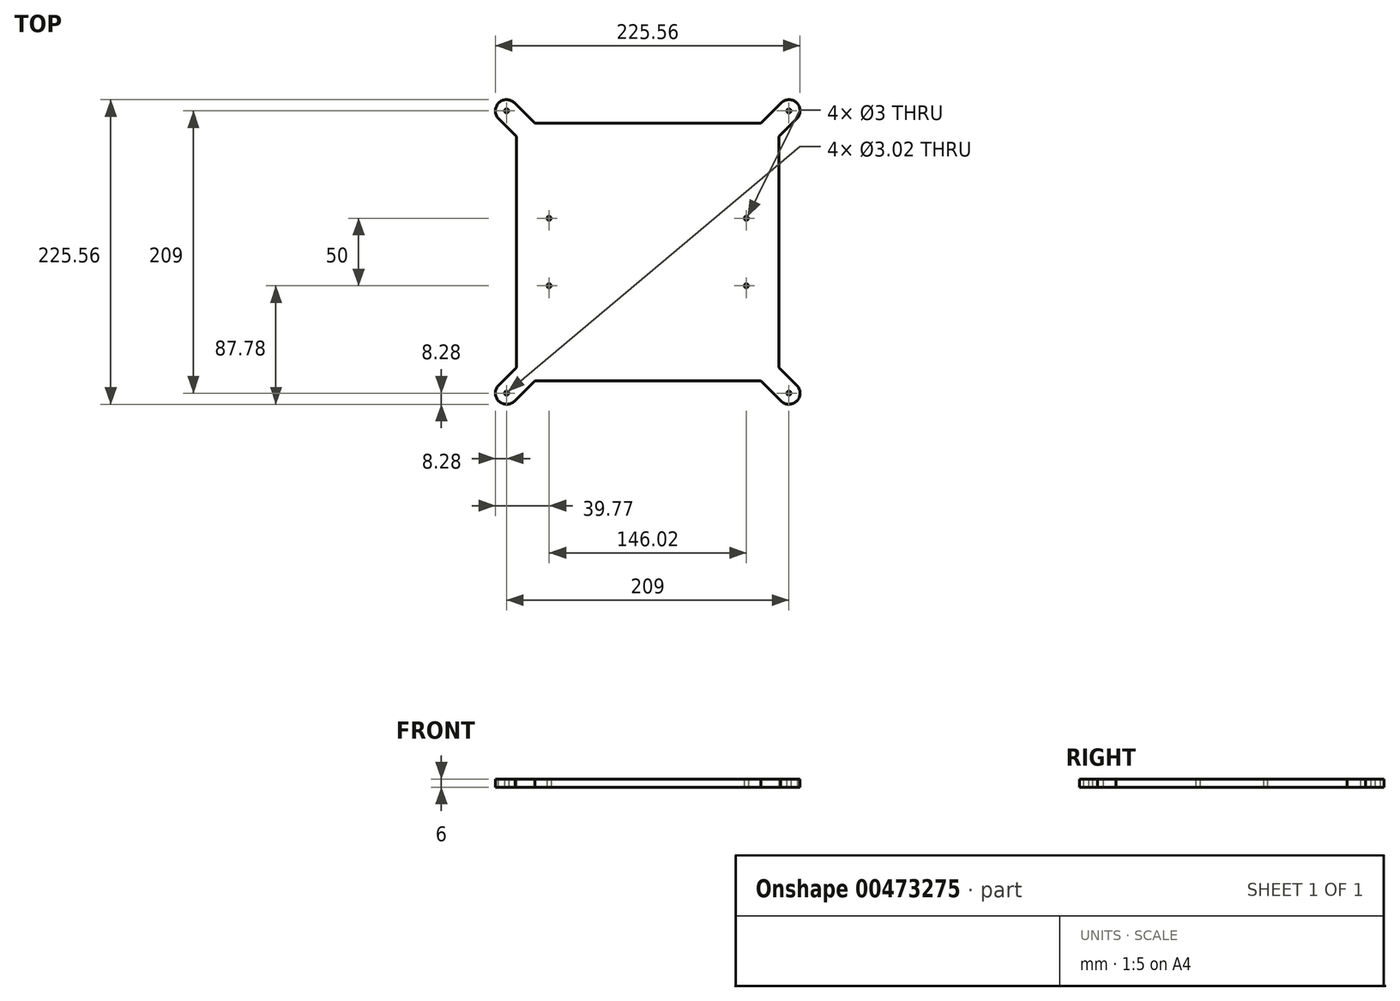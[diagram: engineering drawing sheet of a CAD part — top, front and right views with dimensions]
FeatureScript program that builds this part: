
annotation { "Feature Type Name" : "Feature", "Feature Type Description" : "" }
export const myFeature = defineFeature(function(context is Context, id is Id, definition is map)
    precondition{}
    {
        {
            var Q0;
            Q0=qCreatedBy(makeId("Top.planeOp"), FACE);
            var sketch = newSketch(context, id + "F0", { "sketchPlane" : qUnion([Q0])});
            skLineSegment(sketch, "E0", {"start": v(0, 107.15) * mm, "end": v(0, -107.15) * mm, "construction": true});
            skCircle(sketch, "E1", {"center": v(-104.5, 104.5) * mm, "radius": 1.5 * mm});
            skLineSegment(sketch, "E2", {"start": v(-83.64, 95.33) * mm, "end": v(0, 95.33) * mm});
            skCircle(sketch, "E3", {"center": v(-73, 25) * mm, "radius": 1.5 * mm});
            skLineSegment(sketch, "E4", {"start": v(0, 0) * mm, "end": v(-97.26, 0) * mm, "construction": true});
            skLineSegment(sketch, "E5", {"start": v(-97.26, 85.6) * mm, "end": v(-97.26, 0) * mm});
            skLineSegment(sketch, "E6", {"start": v(-97.26, 85.6) * mm, "end": v(-110.88, 99.22) * mm});
            skLineSegment(sketch, "E7", {"start": v(-83.64, 95.33) * mm, "end": v(-99.03, 110.71) * mm});
            skArc(sketch, "E8", {"start": v(-110.88, 99.22) * mm, "mid": v(-109.88, 110.8) * mm, "end": v(-98.29, 109.97) * mm});
            skCircle(sketch, "E9.MirrorC", {"center": v(-104.5, -104.5) * mm, "radius": 1.5 * mm});
            skCircle(sketch, "E10.MirrorC", {"center": v(-73, -25) * mm, "radius": 1.5 * mm});
            skLineSegment(sketch, "E11.MirrorCS", {"start": v(-97.26, -85.6) * mm, "end": v(-97.26, 0) * mm});
            skArc(sketch, "E12.MirrorCS", {"start": v(-110.88, -99.22) * mm, "mid": v(-109.88, -110.8) * mm, "end": v(-98.29, -109.97) * mm});
            skLineSegment(sketch, "E13.MirrorCS", {"start": v(-83.64, -95.33) * mm, "end": v(-99.03, -110.71) * mm});
            skLineSegment(sketch, "E14.MirrorCS", {"start": v(-83.64, -95.33) * mm, "end": v(0, -95.33) * mm});
            skLineSegment(sketch, "E15.MirrorCS", {"start": v(-97.26, -85.6) * mm, "end": v(-110.88, -99.22) * mm});
            skCircle(sketch, "E16.MirrorC", {"center": v(104.5, -104.5) * mm, "radius": 1.5 * mm});
            skCircle(sketch, "E17.MirrorC", {"center": v(104.5, 104.5) * mm, "radius": 1.5 * mm});
            skCircle(sketch, "E18.MirrorC", {"center": v(73.01, -25) * mm, "radius": 1.5 * mm});
            skCircle(sketch, "E19.MirrorC", {"center": v(73.01, 25) * mm, "radius": 1.5 * mm});
            skLineSegment(sketch, "E20.MirrorCS", {"start": v(97.26, -85.6) * mm, "end": v(97.26, 0) * mm});
            skLineSegment(sketch, "E21.MirrorCS", {"start": v(83.64, -95.33) * mm, "end": v(0, -95.33) * mm});
            skLineSegment(sketch, "E22.MirrorCS", {"start": v(83.64, 95.33) * mm, "end": v(0, 95.33) * mm});
            skLineSegment(sketch, "E23.MirrorCS", {"start": v(97.26, 85.6) * mm, "end": v(110.88, 99.22) * mm});
            skArc(sketch, "E24.MirrorCS", {"start": v(110.88, 99.22) * mm, "mid": v(109.88, 110.8) * mm, "end": v(98.29, 109.97) * mm});
            skLineSegment(sketch, "E25.MirrorCS", {"start": v(83.64, 95.33) * mm, "end": v(99.03, 110.71) * mm});
            skLineSegment(sketch, "E26.MirrorCS", {"start": v(0, 0) * mm, "end": v(97.26, 0) * mm, "construction": true});
            skLineSegment(sketch, "E27.MirrorCS", {"start": v(97.26, 85.6) * mm, "end": v(97.26, 0) * mm});
            skLineSegment(sketch, "E28.MirrorCS", {"start": v(97.26, -85.6) * mm, "end": v(110.88, -99.22) * mm});
            skArc(sketch, "E29.MirrorCS", {"start": v(110.88, -99.22) * mm, "mid": v(109.88, -110.8) * mm, "end": v(98.29, -109.97) * mm});
            skLineSegment(sketch, "E30.MirrorCS", {"start": v(83.64, -95.33) * mm, "end": v(99.03, -110.71) * mm});
            skSolve(sketch);
        }
        {
            var Q0;
            Q0 = qSketchRegion(id + "F0", true);
            extrude(context, id + "F1", {"entities" : qUnion([Q0]), "depth" : 6 * mm, "offsetDistance" : 25 * mm});
        }
    });
